# Revit family: FU_Sofa_Sandler_Krosa 7-3
name_source: partatom
category: Furniture
units: mm (PartAtom-declared; Revit-internal decimal feet)

## family parameters
Always vertical = Yes
Cut with Voids When Loaded = No
OmniClass Number = 23.40.20.00
OmniClass Title = General Furniture and Specialties
Render Appearance Source = Family Geometry
Room Calculation Point = No
Shared = No
Work Plane-Based = No

## types (1)
- Krosa 7.3
    Default Elevation = 0 mm  [stored 0 ft]
    Depth = 880 mm  [stored 2.88714 ft]
    Description = Three-seat sofa with generous cushioning and proportions. Fully upholstered.
    Height = 770 mm  [stored 2.52625 ft]
    Manufacturer = Sandler
    Model = Krose 7.3
    URL = https://www.sandlerseating.com
    Width = 2790 mm  [stored 9.15354 ft]

note: [stored X ft] marks values corroborated as IEEE doubles in the binary element streams (Revit-internal decimal feet)

## geometry (parser evidence)
native form markers: Sweep x2
no freeform markers — native parametric forms only
